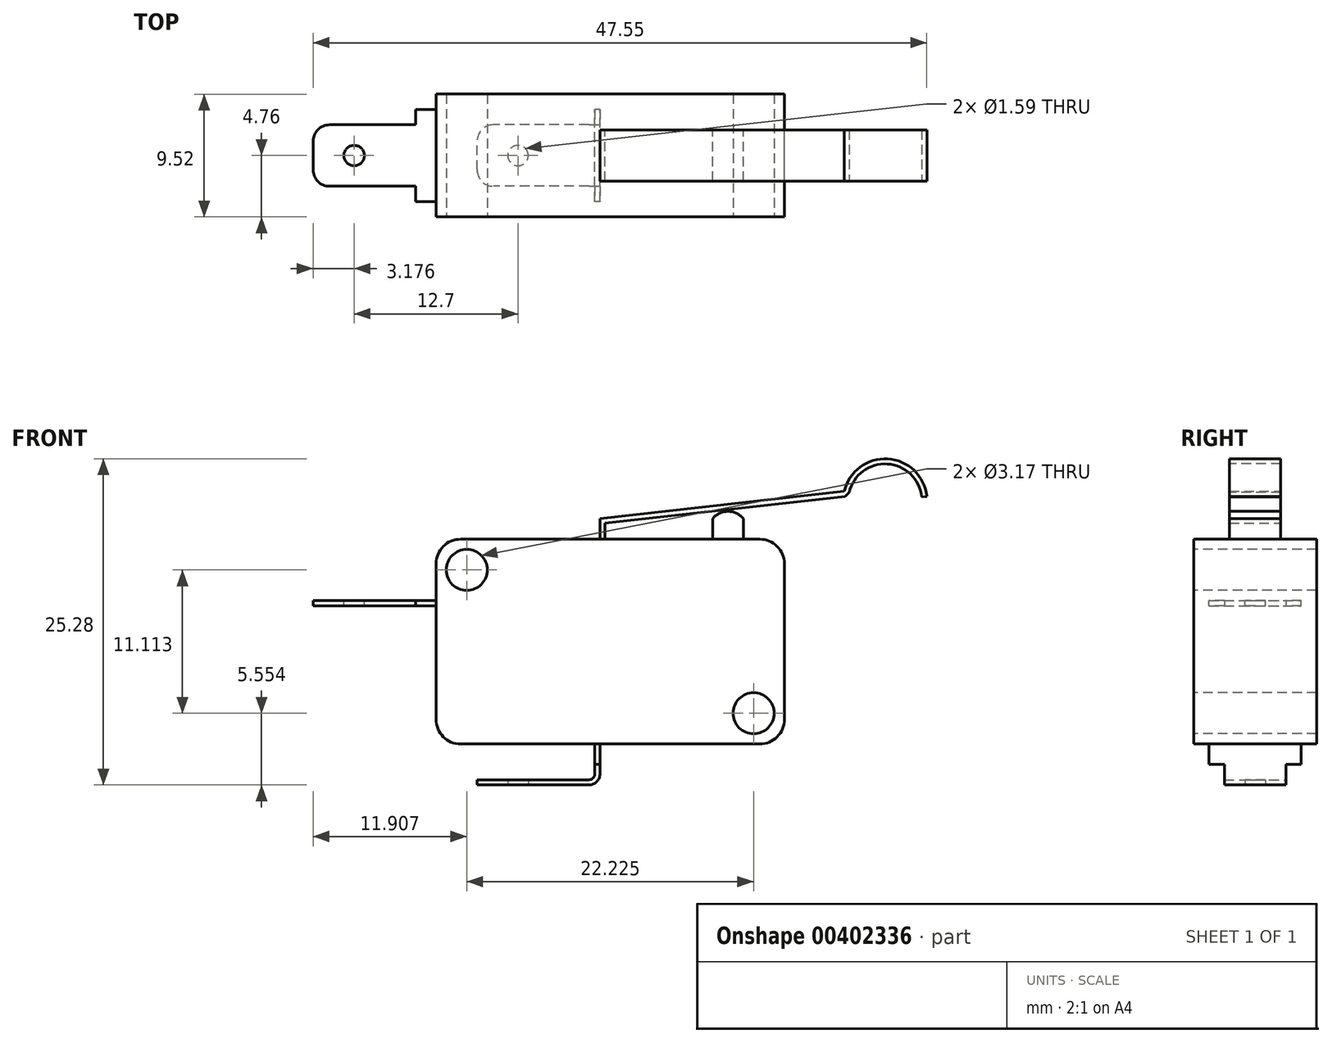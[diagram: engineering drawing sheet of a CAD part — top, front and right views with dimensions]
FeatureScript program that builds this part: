
annotation { "Feature Type Name" : "Feature", "Feature Type Description" : "" }
export const myFeature = defineFeature(function(context is Context, id is Id, definition is map)
    precondition{}
    {
        {
            var Q0;
            Q0=qCreatedBy(makeId("Front.planeOp"),FACE);
            var sketch = newSketch(context, id + "F0", { "sketchPlane" : qUnion([Q0])});
            skLineSegment(sketch, "E0.bottom", {"start": v(13.5, 7.94) * mm, "end": v(-13.5, 7.94) * mm});
            skLineSegment(sketch, "E0.top", {"start": v(13.5, -7.94) * mm, "end": v(-13.5, -7.94) * mm});
            skLineSegment(sketch, "E0.left", {"start": v(13.5, 7.94) * mm, "end": v(13.5, -7.94) * mm});
            skLineSegment(sketch, "E0.right", {"start": v(-13.5, 7.94) * mm, "end": v(-13.5, -7.94) * mm});
            skPoint(sketch, "E0.middle", {"position": v(0, 0) * mm});
            skSolve(sketch);
        }
        {
            var Q0;
            Q0 = qSketchRegion(id + "F0", true);
            extrude(context, id + "F1", {"entities" : qUnion([Q0]), "depth" : 9.52 * mm, "symmetric" : true});
        }
        {
            var Q0;
            Q0=qCreatedBy(makeId("Front.planeOp"),FACE);
            var sketch = newSketch(context, id + "F2", { "sketchPlane" : qUnion([Q0])});
            skLineSegment(sketch, "E1.0", {"start": v(13.5, 7.94) * mm, "end": v(-13.5, 7.94) * mm, "construction": true});
            skLineSegment(sketch, "E2", {"start": v(-0.8, 7.94) * mm, "end": v(-0.8, 9.53) * mm});
            skLineSegment(sketch, "E3", {"start": v(-0.8, 9.53) * mm, "end": v(18.14, 11.65) * mm});
            skLineSegment(sketch, "E4", {"start": v(18.14, 11.65) * mm, "end": v(18.18, 11.26) * mm});
            skLineSegment(sketch, "E5", {"start": v(18.18, 11.26) * mm, "end": v(-0.4, 9.17) * mm});
            skLineSegment(sketch, "E6", {"start": v(-0.4, 9.17) * mm, "end": v(-0.4, 7.94) * mm});
            skLineSegment(sketch, "E7", {"start": v(-0.4, 7.94) * mm, "end": v(-0.8, 7.94) * mm});
            skSolve(sketch);
        }
        {
            var Q0;
            Q0 = qSketchRegion(id + "F2", true);
            extrude(context, id + "F3", {"entities" : qUnion([Q0]), "operationType" : NewBodyOperationType.ADD, "depth" : 3.97 * mm, "symmetric" : true});
        }
        {
            var Q0;
            Q0=makeQuery(id+"F3.opExtrude","CAP_FACE",FACE,{"disambiguationData":[OSD([sQuery(id+"F2.wireOp",EDGE,"E2"),sQuery(id+"F2.wireOp",EDGE,"E3"),sQuery(id+"F2.wireOp",EDGE,"E4"),sQuery(id+"F2.wireOp",EDGE,"E5"),sQuery(id+"F2.wireOp",EDGE,"E6"),sQuery(id+"F2.wireOp",EDGE,"E7")])],"isStart":false});
            var sketch = newSketch(context, id + "F4", { "sketchPlane" : qUnion([Q0])});
            skArc(sketch, "E8", {"start": v(24.53, 11.26) * mm, "mid": v(21.5, 14.17) * mm, "end": v(18.14, 11.65) * mm});
            skLineSegment(sketch, "E9", {"start": v(18.18, 11.26) * mm, "end": v(27.02, 11.26) * mm, "construction": true});
            skArc(sketch, "E10.0", {"start": v(24.14, 11.22) * mm, "mid": v(21.48, 13.77) * mm, "end": v(18.52, 11.57) * mm});
            skLineSegment(sketch, "E11", {"start": v(18.52, 11.57) * mm, "end": v(18.18, 11.26) * mm});
            skLineSegment(sketch, "E12", {"start": v(18.18, 11.26) * mm, "end": v(18.14, 11.65) * mm});
            skLineSegment(sketch, "E13", {"start": v(24.14, 11.22) * mm, "end": v(24.53, 11.26) * mm});
            skSolve(sketch);
        }
        {
            var Q0;
            Q0 = qSketchRegion(id + "F4", true);
            var Q1;
            Q1=makeQuery(id+"F3.opExtrude","CAP_FACE",FACE,{"disambiguationData":[OSD([sQuery(id+"F2.wireOp",EDGE,"E2"),sQuery(id+"F2.wireOp",EDGE,"E3"),sQuery(id+"F2.wireOp",EDGE,"E4"),sQuery(id+"F2.wireOp",EDGE,"E5"),sQuery(id+"F2.wireOp",EDGE,"E6"),sQuery(id+"F2.wireOp",EDGE,"E7")])],"isStart":true});
            extrude(context, id + "F5", {"entities" : qUnion([Q0]), "operationType" : NewBodyOperationType.ADD, "endBound" : BoundingType.UP_TO_SURFACE, "oppositeDirection" : true, "endBoundEntityFace" : qUnion([Q1]), "depth" : 25.4 * mm});
        }
        {
            var Q0;
            Q0=qCreatedBy(makeId("Front.planeOp"),FACE);
            var sketch = newSketch(context, id + "F6", { "sketchPlane" : qUnion([Q0])});
            skLineSegment(sketch, "E14.0", {"start": v(13.5, 7.94) * mm, "end": v(-13.5, 7.94) * mm, "construction": true});
            skLineSegment(sketch, "E15.bottom", {"start": v(10.32, 7.94) * mm, "end": v(7.94, 7.94) * mm});
            skLineSegment(sketch, "E15.left", {"start": v(10.32, 7.94) * mm, "end": v(10.32, 9.53) * mm});
            skLineSegment(sketch, "E15.right", {"start": v(7.94, 7.94) * mm, "end": v(7.94, 9.53) * mm});
            skArc(sketch, "E16", {"start": v(10.32, 9.53) * mm, "mid": v(9.13, 10.1) * mm, "end": v(7.94, 9.53) * mm});
            skSolve(sketch);
        }
        {
            var Q0;
            Q0 = qSketchRegion(id + "F6", true);
            extrude(context, id + "F7", {"entities" : qUnion([Q0]), "operationType" : NewBodyOperationType.ADD, "depth" : 3.97 * mm, "symmetric" : true});
        }
        {
            var Q0;
            Q0=qCreatedBy(makeId("Front.planeOp"),FACE);
            var sketch = newSketch(context, id + "F8", { "sketchPlane" : qUnion([Q0])});
            skLineSegment(sketch, "E17.0", {"start": v(-13.5, 7.94) * mm, "end": v(-13.5, -7.94) * mm, "construction": true});
            skLineSegment(sketch, "E18.bottom", {"start": v(-13.5, 3.18) * mm, "end": v(-23.02, 3.18) * mm});
            skLineSegment(sketch, "E18.top", {"start": v(-13.5, 2.78) * mm, "end": v(-23.02, 2.78) * mm});
            skLineSegment(sketch, "E18.left", {"start": v(-13.5, 3.18) * mm, "end": v(-13.5, 2.78) * mm});
            skLineSegment(sketch, "E18.right", {"start": v(-23.02, 3.18) * mm, "end": v(-23.02, 2.78) * mm});
            skSolve(sketch);
        }
        {
            var Q0;
            Q0 = qSketchRegion(id + "F8", true);
            extrude(context, id + "F9", {"entities" : qUnion([Q0]), "operationType" : NewBodyOperationType.ADD, "depth" : 4.76 * mm, "symmetric" : true});
        }
        {
            var Q0;
            Q0=makeQuery(id+"F9.opExtrude","SWEPT_FACE",FACE,{"disambiguationData":[OSD([sQuery(id+"F8.wireOp",EDGE,"E18.bottom")])]});
            var sketch = newSketch(context, id + "F10", { "sketchPlane" : qUnion([Q0])});
            skLineSegment(sketch, "E19.0", {"start": v(-13.5, -4.76) * mm, "end": v(-13.5, 4.76) * mm, "construction": true});
            skLineSegment(sketch, "E20.bottom", {"start": v(-13.5, 3.57) * mm, "end": v(-15.08, 3.57) * mm});
            skLineSegment(sketch, "E20.top", {"start": v(-13.5, -3.57) * mm, "end": v(-15.08, -3.57) * mm});
            skLineSegment(sketch, "E20.left", {"start": v(-13.5, 3.57) * mm, "end": v(-13.5, -3.57) * mm});
            skLineSegment(sketch, "E20.right", {"start": v(-15.08, 3.57) * mm, "end": v(-15.08, -3.57) * mm});
            skSolve(sketch);
        }
        {
            var Q0;
            Q0 = qSketchRegion(id + "F10", true);
            var Q1;
            Q1=makeQuery(id+"F9.opExtrude","SWEPT_FACE",FACE,{"disambiguationData":[OSD([sQuery(id+"F8.wireOp",EDGE,"E18.top")])]});
            extrude(context, id + "F11", {"entities" : qUnion([Q0]), "operationType" : NewBodyOperationType.ADD, "endBound" : BoundingType.UP_TO_SURFACE, "oppositeDirection" : true, "endBoundEntityFace" : qUnion([Q1]), "depth" : 25.4 * mm});
        }
        {
            var Q0;
            Q0=makeQuery(id+"F11.boolean.opBoolean","MERGE",FACE,{"derivedFrom":[makeQuery(id+"F9.opExtrude","SWEPT_FACE",FACE,{"disambiguationData":[OSD([sQuery(id+"F8.wireOp",EDGE,"E18.bottom")])]}),makeQuery(id+"F11.opExtrude","CAP_FACE",FACE,{"disambiguationData":[OSD([sQuery(id+"F10.wireOp",EDGE,"E20.bottom"),sQuery(id+"F10.wireOp",EDGE,"E20.top"),sQuery(id+"F10.wireOp",EDGE,"E20.left"),sQuery(id+"F10.wireOp",EDGE,"E20.right")])],"isStart":true})]});
            var sketch = newSketch(context, id + "F12", { "sketchPlane" : qUnion([Q0])});
            skCircle(sketch, "E21", {"center": v(-19.84, 0) * mm, "radius": 0.8 * mm});
            skSolve(sketch);
        }
        {
            var Q0;
            Q0 = qSketchRegion(id + "F12", true);
            extrude(context, id + "F13", {"entities" : qUnion([Q0]), "operationType" : NewBodyOperationType.REMOVE, "endBound" : BoundingType.THROUGH_ALL, "oppositeDirection" : true, "depth" : 25.4 * mm});
        }
        {
            var Q0;
            Q0=makeQuery(id+"F9.opExtrude","CAP_EDGE",EDGE,{"disambiguationData":[OSD([sQuery(id+"F8.wireOp",EDGE,"E18.right")])],"isStart":false});
            var Q1;
            Q1=makeQuery(id+"F9.opExtrude","CAP_EDGE",EDGE,{"disambiguationData":[OSD([sQuery(id+"F8.wireOp",EDGE,"E18.right")])],"isStart":true});
            fillet(context, id + "F14", {"entities" : qUnion([Q0, Q1]), "radius" : 1.27 * mm, "tangentPropagation" : true, "allowEdgeOverflow" : false});
        }
        {
            var Q0;
            Q0=qCreatedBy(makeId("Front.planeOp"),FACE);
            var sketch = newSketch(context, id + "F15", { "sketchPlane" : qUnion([Q0])});
            skLineSegment(sketch, "E22.0", {"start": v(-0.8, 7.94) * mm, "end": v(-0.8, 9.53) * mm, "construction": true});
            skLineSegment(sketch, "E23.0", {"start": v(13.5, -7.94) * mm, "end": v(-13.5, -7.94) * mm, "construction": true});
            skLineSegment(sketch, "E24", {"start": v(-0.8, -7.94) * mm, "end": v(-0.8, -10.25) * mm});
            skLineSegment(sketch, "E25", {"start": v(-1.66, -11.11) * mm, "end": v(-10.32, -11.11) * mm});
            skPoint(sketch, "E26.visualSharp", {"position": v(-0.8, -11.11) * mm});
            skArc(sketch, "E26.filletArc", {"start": v(-1.66, -11.11) * mm, "mid": v(-1.05, -10.86) * mm, "end": v(-0.8, -10.25) * mm});
            skLineSegment(sketch, "E27.0", {"start": v(-1.2, -7.94) * mm, "end": v(-1.2, -10.25) * mm});
            skArc(sketch, "E28.0", {"start": v(-1.66, -10.72) * mm, "mid": v(-1.33, -10.58) * mm, "end": v(-1.2, -10.25) * mm});
            skLineSegment(sketch, "E29.0", {"start": v(-1.66, -10.72) * mm, "end": v(-10.32, -10.72) * mm});
            skLineSegment(sketch, "E30", {"start": v(-10.32, -10.72) * mm, "end": v(-10.32, -11.11) * mm});
            skLineSegment(sketch, "E31", {"start": v(-1.2, -7.94) * mm, "end": v(-0.8, -7.94) * mm});
            skSolve(sketch);
        }
        {
            var Q0;
            Q0 = qSketchRegion(id + "F15", true);
            extrude(context, id + "F16", {"entities" : qUnion([Q0]), "operationType" : NewBodyOperationType.ADD, "depth" : 4.76 * mm, "symmetric" : true});
        }
        {
            var Q0;
            Q0=makeQuery(id+"F16.opExtrude","SWEPT_FACE",FACE,{"disambiguationData":[OSD([sQuery(id+"F15.wireOp",EDGE,"E27.0")])]});
            var sketch = newSketch(context, id + "F17", { "sketchPlane" : qUnion([Q0])});
            skLineSegment(sketch, "E32.0", {"start": v(4.76, -7.94) * mm, "end": v(-4.76, -7.94) * mm, "construction": true});
            skLineSegment(sketch, "E33.bottom", {"start": v(-3.57, -7.94) * mm, "end": v(3.57, -7.94) * mm});
            skLineSegment(sketch, "E33.top", {"start": v(-3.57, -9.52) * mm, "end": v(3.57, -9.52) * mm});
            skLineSegment(sketch, "E33.left", {"start": v(-3.57, -7.94) * mm, "end": v(-3.57, -9.52) * mm});
            skLineSegment(sketch, "E33.right", {"start": v(3.57, -7.94) * mm, "end": v(3.57, -9.52) * mm});
            skSolve(sketch);
        }
        {
            var Q0;
            Q0 = qSketchRegion(id + "F17", true);
            var Q1;
            Q1=makeQuery(id+"F16.opExtrude","SWEPT_FACE",FACE,{"disambiguationData":[OSD([sQuery(id+"F15.wireOp",EDGE,"E24")])]});
            extrude(context, id + "F18", {"entities" : qUnion([Q0]), "operationType" : NewBodyOperationType.ADD, "endBound" : BoundingType.UP_TO_SURFACE, "oppositeDirection" : true, "endBoundEntityFace" : qUnion([Q1]), "depth" : 25.4 * mm});
        }
        {
            var Q0;
            Q0=makeQuery(id+"F16.opExtrude","SWEPT_FACE",FACE,{"disambiguationData":[OSD([sQuery(id+"F15.wireOp",EDGE,"E25")])]});
            var sketch = newSketch(context, id + "F19", { "sketchPlane" : qUnion([Q0])});
            skCircle(sketch, "E34", {"center": v(-7.14, 0) * mm, "radius": 0.8 * mm});
            skLineSegment(sketch, "E35.0", {"start": v(-0.8, 2.38) * mm, "end": v(-0.8, -2.38) * mm, "construction": true});
            skSolve(sketch);
        }
        {
            var Q0;
            Q0 = qSketchRegion(id + "F19", true);
            extrude(context, id + "F20", {"entities" : qUnion([Q0]), "operationType" : NewBodyOperationType.REMOVE, "endBound" : BoundingType.UP_TO_NEXT, "oppositeDirection" : true, "depth" : 25.4 * mm});
        }
        {
            var Q0;
            Q0=makeQuery(id+"F16.opExtrude","CAP_EDGE",EDGE,{"disambiguationData":[OSD([sQuery(id+"F15.wireOp",EDGE,"E30")])],"isStart":true});
            var Q1;
            Q1=makeQuery(id+"F16.opExtrude","CAP_EDGE",EDGE,{"disambiguationData":[OSD([sQuery(id+"F15.wireOp",EDGE,"E30")])],"isStart":false});
            fillet(context, id + "F21", {"entities" : qUnion([Q0, Q1]), "radius" : 1.27 * mm, "tangentPropagation" : true, "allowEdgeOverflow" : false});
        }
        {
            var Q0;
            Q0=makeQuery(id+"F1.opExtrude","CAP_FACE",FACE,{"disambiguationData":[OSD([sQuery(id+"F0.wireOp",EDGE,"E0.bottom"),sQuery(id+"F0.wireOp",EDGE,"E0.top"),sQuery(id+"F0.wireOp",EDGE,"E0.left"),sQuery(id+"F0.wireOp",EDGE,"E0.right")])],"isStart":false});
            var sketch = newSketch(context, id + "F22", { "sketchPlane" : qUnion([Q0])});
            skCircle(sketch, "E36", {"center": v(-11.11, 5.56) * mm, "radius": 1.59 * mm});
            skSolve(sketch);
        }
        {
            var Q0;
            Q0 = qSketchRegion(id + "F22", true);
            extrude(context, id + "F23", {"entities" : qUnion([Q0]), "operationType" : NewBodyOperationType.REMOVE, "endBound" : BoundingType.THROUGH_ALL, "oppositeDirection" : true, "depth" : 25.4 * mm});
        }
        {
            var Q0;
            Q0=makeQuery(id+"F1.opExtrude","CAP_FACE",FACE,{"disambiguationData":[OSD([sQuery(id+"F0.wireOp",EDGE,"E0.bottom"),sQuery(id+"F0.wireOp",EDGE,"E0.top"),sQuery(id+"F0.wireOp",EDGE,"E0.left"),sQuery(id+"F0.wireOp",EDGE,"E0.right")])],"isStart":false});
            var sketch = newSketch(context, id + "F24", { "sketchPlane" : qUnion([Q0])});
            skCircle(sketch, "E37", {"center": v(11.11, -5.56) * mm, "radius": 1.59 * mm});
            skSolve(sketch);
        }
        {
            var Q0;
            Q0 = qSketchRegion(id + "F24", true);
            extrude(context, id + "F25", {"entities" : qUnion([Q0]), "operationType" : NewBodyOperationType.REMOVE, "endBound" : BoundingType.THROUGH_ALL, "oppositeDirection" : true, "depth" : 25.4 * mm});
        }
        {
            var Q0;
            Q0=makeQuery(id+"F1.opExtrude","SWEPT_EDGE",EDGE,{"disambiguationData":[OSD([sQuery(id+"F0.wireOp",EDGE,"E0.bottom"),sQuery(id+"F0.wireOp",EDGE,"E0.right")])]});
            var Q1;
            Q1=makeQuery(id+"F1.opExtrude","SWEPT_EDGE",EDGE,{"disambiguationData":[OSD([sQuery(id+"F0.wireOp",EDGE,"E0.bottom"),sQuery(id+"F0.wireOp",EDGE,"E0.left")])]});
            var Q2;
            Q2=makeQuery(id+"F1.opExtrude","SWEPT_EDGE",EDGE,{"disambiguationData":[OSD([sQuery(id+"F0.wireOp",EDGE,"E0.top"),sQuery(id+"F0.wireOp",EDGE,"E0.left")])]});
            var Q3;
            Q3=makeQuery(id+"F1.opExtrude","SWEPT_EDGE",EDGE,{"disambiguationData":[OSD([sQuery(id+"F0.wireOp",EDGE,"E0.top"),sQuery(id+"F0.wireOp",EDGE,"E0.right")])]});
            fillet(context, id + "F26", {"entities" : qUnion([Q0, Q1, Q2, Q3]), "radius" : 1.9 * mm, "tangentPropagation" : true, "allowEdgeOverflow" : false});
        }
    });
